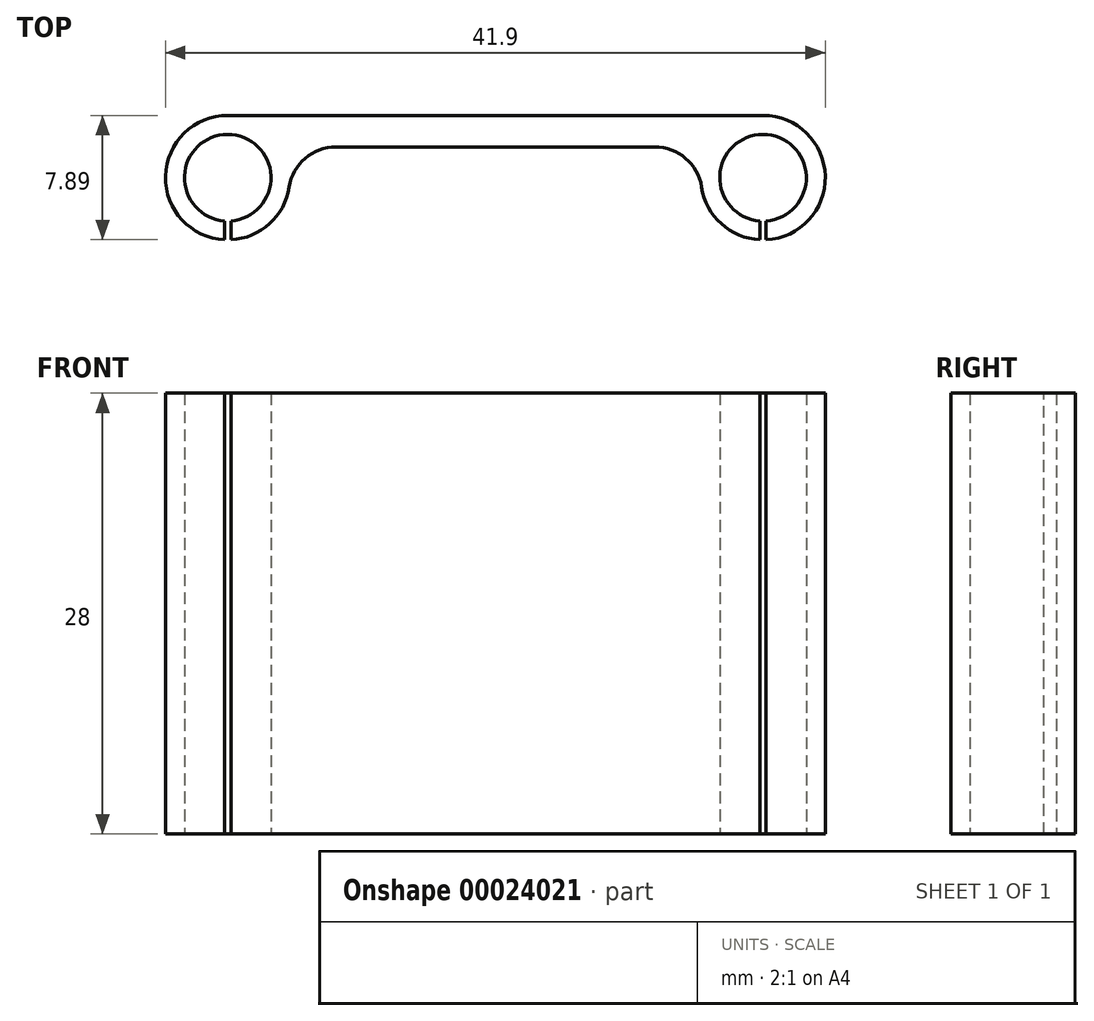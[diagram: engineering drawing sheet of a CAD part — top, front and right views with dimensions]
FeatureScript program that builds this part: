
annotation { "Feature Type Name" : "Feature", "Feature Type Description" : "" }
export const myFeature = defineFeature(function(context is Context, id is Id, definition is map)
    precondition{}
    {
        {
            var Q0;
            Q0=qCreatedBy(makeId("Top.planeOp"),FACE);
            var sketch = newSketch(context, id + "F0", { "sketchPlane" : qUnion([Q0])});
            skLineSegment(sketch, "E0", {"start": v(0, 0) * mm, "end": v(-34, 0) * mm, "construction": true});
            skCircle(sketch, "E1", {"center": v(-34, 0) * mm, "radius": 2.75 * mm});
            skCircle(sketch, "E2", {"center": v(0, 0) * mm, "radius": 2.75 * mm});
            skCircle(sketch, "E3", {"center": v(-34, 0) * mm, "radius": 3.95 * mm});
            skLineSegment(sketch, "E4", {"start": v(-17, 0) * mm, "end": v(-17, 8.35) * mm, "construction": true});
            skPoint(sketch, "E4.endSnap0", {"position": v(-17, 0) * mm});
            skCircle(sketch, "E5.MirrorC", {"center": v(0, 0) * mm, "radius": 3.95 * mm});
            skLineSegment(sketch, "E6", {"start": v(-34, 3.95) * mm, "end": v(0, 3.95) * mm});
            skLineSegment(sketch, "E7.bottom", {"start": v(-33.8, -2.74) * mm, "end": v(-34.2, -2.74) * mm});
            skLineSegment(sketch, "E7.top", {"start": v(-33.8, -5.16) * mm, "end": v(-34.2, -5.16) * mm});
            skLineSegment(sketch, "E7.left", {"start": v(-33.8, -2.74) * mm, "end": v(-33.8, -5.16) * mm});
            skLineSegment(sketch, "E7.right", {"start": v(-34.2, -2.74) * mm, "end": v(-34.2, -5.16) * mm});
            skPoint(sketch, "E7.middle", {"position": v(-34, -3.95) * mm});
            skLineSegment(sketch, "E8.MirrorCS", {"start": v(0.2, -2.74) * mm, "end": v(0.2, -5.16) * mm});
            skLineSegment(sketch, "E9.MirrorCS", {"start": v(-0.2, -2.74) * mm, "end": v(-0.2, -5.16) * mm});
            skLineSegment(sketch, "E10", {"start": v(-30.56, 1.95) * mm, "end": v(-3.44, 1.95) * mm});
            skSolve(sketch);
        }
        {
            var Q0;
            {var subQ0=sQuery(id+"F0.wireOp",EDGE,"E6");Q0=makeQuery(id+"F0.imprint","IMPRINT",FACE,{"disambiguationData":[TD([[makeQuery(id+"F0.imprint","IMPRINT",EDGE,{"derivedFrom":subQ0}),-1.0]])]});}
            var Q1;
            {var subQ0=sQuery(id+"F0.wireOp",EDGE,"E3");var subQ4=makeQuery(id+"F0.imprint","INTERSECT",VERTEX,{"derivedFrom":[subQ0,sQuery(id+"F0.wireOp",EDGE,"E6")]});Q1=makeQuery(id+"F0.imprint","IMPRINT",FACE,{"disambiguationData":[TD([[makeQuery(id+"F0.imprint","IMPRINT",EDGE,{"disambiguationData":[TD([[subQ4,1.0]])],"derivedFrom":subQ0}),1.0]])]});}
            var Q2;
            {var subQ5=sQuery(id+"F0.wireOp",EDGE,"E8.MirrorCS");var subQ7=sQuery(id+"F0.wireOp",EDGE,"E2");var subQ8=makeQuery(id+"F0.imprint","INTERSECT",VERTEX,{"derivedFrom":[subQ7,subQ5]});Q2=makeQuery(id+"F0.imprint","IMPRINT",FACE,{"disambiguationData":[TD([[makeQuery(id+"F0.imprint","IMPRINT",EDGE,{"disambiguationData":[TD([[subQ8,-1.0]])],"derivedFrom":subQ7}),-1.0]])]});}
            extrude(context, id + "F1", {"entities" : qUnion([Q0, Q1, Q2]), "depth" : 28 * mm});
        }
        {
            var Q0;
            Q0=makeQuery(id+"F1.opExtrude","SWEPT_EDGE",EDGE,{"disambiguationData":[OSD([sQuery(id+"F0.wireOp",EDGE,"E3"),sQuery(id+"F0.wireOp",EDGE,"E10")])]});
            var Q1;
            Q1=makeQuery(id+"F1.opExtrude","SWEPT_EDGE",EDGE,{"disambiguationData":[OSD([sQuery(id+"F0.wireOp",EDGE,"E5.MirrorC"),sQuery(id+"F0.wireOp",EDGE,"E10")])]});
            fillet(context, id + "F2", {"entities" : qUnion([Q0, Q1]), "radius" : 3 * mm, "tangentPropagation" : true, "allowEdgeOverflow" : false});
        }
    });
